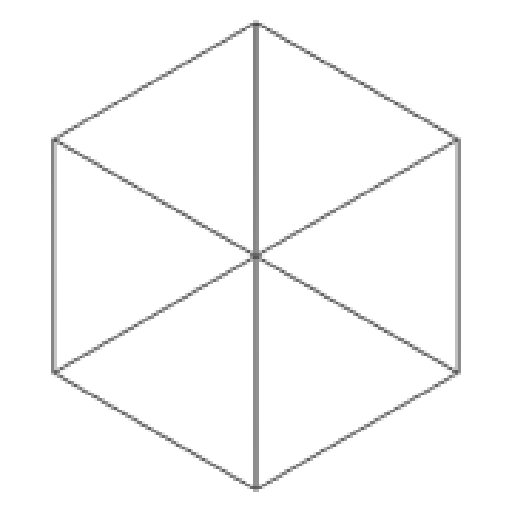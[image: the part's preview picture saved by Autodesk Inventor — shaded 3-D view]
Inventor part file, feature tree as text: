
AUTODESK INVENTOR PART (.ipt)
format: ipt  version: 2023 (Build 270158000, 158)  size: 191,488 bytes
history: native  units: in
note: dims shown in document units (in); Inventor stores cm internally (conversion verified against a paired STEP export)
features: extrude x4, sketch x4, projected_geometry x3, fillet x1
ambient origin geometry x8: Origin, YZ Plane, XZ Plane, XY Plane, X Axis, Y Axis, Z Axis, Center Point
bodies: Solid1 (feature_tree)
feature tree (12):
  extrude  "Extrusion1"  Depth=118.1102in TaperAngle=0.0deg
  extrude  "Extrusion2"  TaperAngle=0.0deg  [1 undecoded]
  extrude  "Extrusion3"  TaperAngle=0.0deg  [1 undecoded]
  extrude  "Extrusion4"  TaperAngle=0.0deg  [1 undecoded]
  fillet  "Fillet1"  Radius=0.25in
  sketch  "Sketch1"  dims[d0=118.1102in d2=118.1102in d3=0.0in]
  sketch  "Sketch2"  dims[d4=1.0in d5=0.0in d6=0.0in]
  projected_geometry  "Projected Loop1"
  sketch  "Sketch3"  dims[d7=1.0in d8=0.0in d9=0.0in]
  projected_geometry  "Projected Loop2"
  sketch  "Sketch4"  dims[d10=1.0in d11=0.0in d12=0.0in d13=0.25in]
  projected_geometry  "Projected Loop3"
note: 3 required parameter values undecoded (feature->parameter linkage not recoverable at this tier; creation-order binding heuristic only, values carry confidence <= 0.55)
